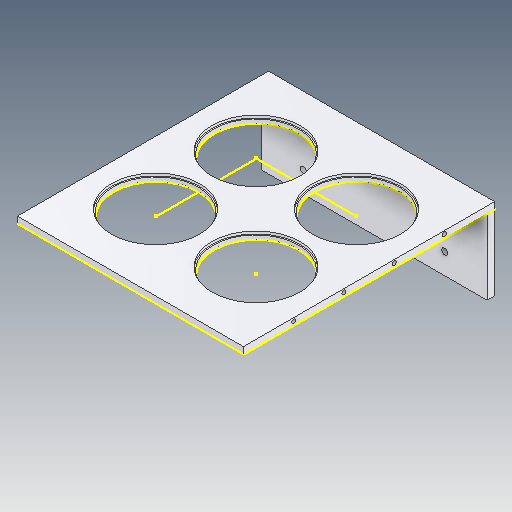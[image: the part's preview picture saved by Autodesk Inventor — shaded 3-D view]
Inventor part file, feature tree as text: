
AUTODESK INVENTOR PART (.ipt)
format: ipt  version: 2020.3 (Build 243373010, 373A)  size: 159,232 bytes
history: native  units: mm
features: sketch x4, other x3
ambient origin geometry x8: Origin, YZ Plane, XZ Plane, XY Plane, X Axis, Y Axis, Z Axis, Center Point
bodies: Solid1 (feature_tree)
feature tree (7):
  other  "LensHolder.ipt"
  other  "Solid1::LensHolder.ipt"
  other  "TaggingFeature1"
  sketch  "Sketch1"  dims[d0=10.0mm]
  sketch  "Sketch2"
  sketch  "Sketch3"
  sketch  "Sketch4"
